# Revit family: Gira_291103
name_source: partatom
category: Electrical Fixtures
revit_build: Autodesk Revit 2017 (Build: 20160225_1515(x64)
units: mm (PartAtom-declared; Revit-internal decimal feet)

## family parameters
Cut with Voids When Loaded = No
Host = Face
Maintain Annotation Orientation = Yes
Part Type = Normal
Room Calculation Point = No
Round Connector Dimension = Use Diameter
Shared = No

## types (1)
- Abstelltaster System 55 Reinweiß
    Art der Spannungsversorgung = Bus-System
    Available = Yes
    Bauart = Wandgerät
    Bedienung = Taste
    Busfähig = 2-Draht
    Category = Ruf-, Bedienervorrichtung Klinikinstallation
    Data sheet (1) = https://katalog.gira.de
    Default Elevation = 1219 mm
    Farbe = weiß
    GTIN = 4010337062349
    Geeignet für = Ruf
    HAN = 291103
    HeinzeBIM = https://bimportal.heinze.de
    Manufacturer URL = https://www.gira.de
    Model = Sys55_Komplettgerät_Schalten und Tasten
    Name = Abstelltaster System 55 Reinweiß
    Region = DE
    Tasterfarbe = grün
    Tasterfunktion = Ruf abstellen
    URL = http://katalog.gira.de
    Werkstoff = sonstige
    Werkstoffgüte = sonstige
    Zusammenstellung = Basiselement

## geometry (parser evidence)
native form markers: Blend x2, Sweep x9
no freeform markers — native parametric forms only
